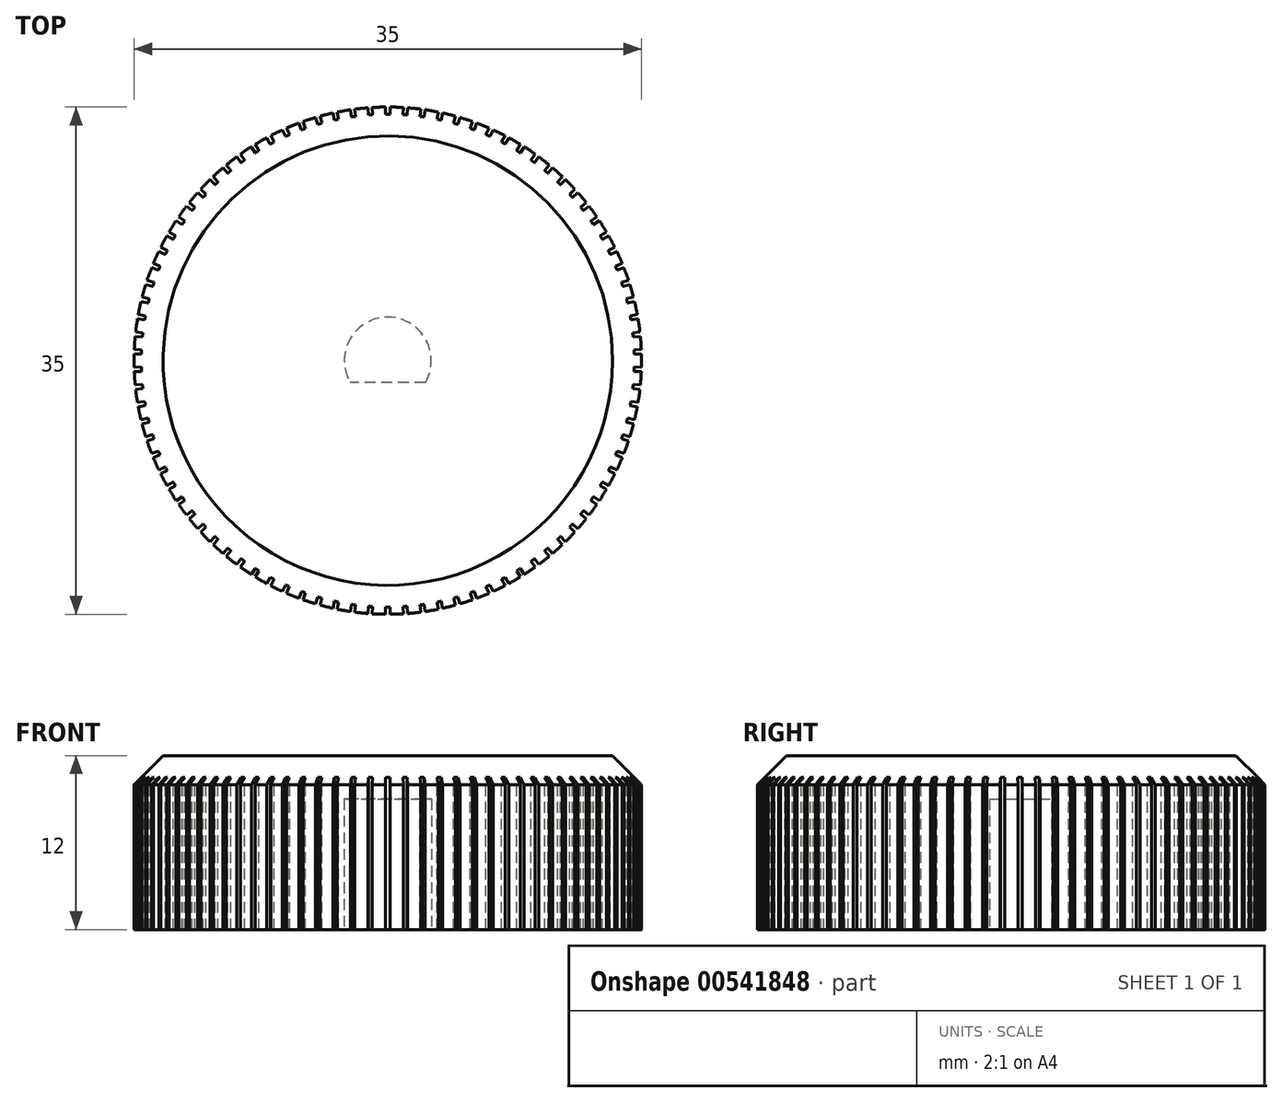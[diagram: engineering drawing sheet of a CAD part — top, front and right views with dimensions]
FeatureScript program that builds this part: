
annotation { "Feature Type Name" : "Feature", "Feature Type Description" : "" }
export const myFeature = defineFeature(function(context is Context, id is Id, definition is map)
    precondition{}
    {
        {
            var Q0;
            Q0=qCreatedBy(makeId("Top.planeOp"),FACE);
            var sketch = newSketch(context, id + "F0", { "sketchPlane" : qUnion([Q0])});
            skCircle(sketch, "E0", {"center": v(0, 0) * mm, "radius": 17.5 * mm});
            skSolve(sketch);
        }
        {
            var Q0;
            Q0=makeQuery(id+"F0.imprint","IMPRINT",FACE,{"disambiguationData":[TD([[makeQuery(id+"F0.imprint","IMPRINT",EDGE,{"derivedFrom":sQuery(id+"F0.wireOp",EDGE,"E0")}),1.0]])]});
            extrude(context, id + "F1", {"entities" : qUnion([Q0]), "depth" : 12 * mm, "offsetDistance" : 25 * mm});
        }
        {
            var Q0;
            Q0=makeQuery(id+"F1.opExtrude","CAP_EDGE",EDGE,{"disambiguationData":[OSD([sQuery(id+"F0.wireOp",EDGE,"E0")])],"isStart":false});
            chamfer(context, id + "F2", {"entities" : qUnion([Q0]), "width" : 2 * mm, "tangentPropagation" : true});
        }
        {
            var Q0;
            Q0=makeQuery(id+"F1.opExtrude","CAP_FACE",FACE,{"disambiguationData":[OSD([sQuery(id+"F0.wireOp",EDGE,"E0")])],"isStart":false});
            var sketch = newSketch(context, id + "F3", { "sketchPlane" : qUnion([Q0])});
            skLineSegment(sketch, "E1", {"start": v(0.15, 17) * mm, "end": v(0.17, 20) * mm});
            skLineSegment(sketch, "E2", {"start": v(0.17, 20) * mm, "end": v(-0.17, 20) * mm});
            skLineSegment(sketch, "E3", {"start": v(-0.17, 20) * mm, "end": v(-0.15, 17) * mm});
            skLineSegment(sketch, "E4.1.2", {"start": v(-0.17, -20) * mm, "end": v(0.17, -20) * mm});
            skPoint(sketch, "E4.center", {"position": v(0, 0) * mm});
            skLineSegment(sketch, "E5", {"start": v(0.15, 17) * mm, "end": v(-0.15, 17) * mm});
            skLineSegment(sketch, "E6.1.0", {"start": v(-1.04, 16.97) * mm, "end": v(-1.22, 19.96) * mm});
            skLineSegment(sketch, "E6.1.1", {"start": v(-1.04, 16.97) * mm, "end": v(-1.33, 16.95) * mm});
            skLineSegment(sketch, "E6.1.2", {"start": v(-1.57, 19.94) * mm, "end": v(-1.33, 16.95) * mm});
            skLineSegment(sketch, "E6.1.3", {"start": v(-1.22, 19.96) * mm, "end": v(-1.57, 19.94) * mm});
            skLineSegment(sketch, "E6.2.0", {"start": v(-2.22, 16.85) * mm, "end": v(-2.61, 19.83) * mm});
            skLineSegment(sketch, "E6.2.1", {"start": v(-2.22, 16.85) * mm, "end": v(-2.51, 16.82) * mm});
            skLineSegment(sketch, "E6.2.2", {"start": v(-2.96, 19.78) * mm, "end": v(-2.51, 16.82) * mm});
            skLineSegment(sketch, "E6.2.3", {"start": v(-2.61, 19.83) * mm, "end": v(-2.96, 19.78) * mm});
            skLineSegment(sketch, "E6.3.0", {"start": v(-3.39, 16.66) * mm, "end": v(-3.99, 19.6) * mm});
            skLineSegment(sketch, "E6.3.1", {"start": v(-3.39, 16.66) * mm, "end": v(-3.68, 16.6) * mm});
            skLineSegment(sketch, "E6.3.2", {"start": v(-4.33, 19.53) * mm, "end": v(-3.68, 16.6) * mm});
            skLineSegment(sketch, "E6.3.3", {"start": v(-3.99, 19.6) * mm, "end": v(-4.33, 19.53) * mm});
            skLineSegment(sketch, "E6.4.0", {"start": v(-4.54, 16.38) * mm, "end": v(-5.34, 19.27) * mm});
            skLineSegment(sketch, "E6.4.1", {"start": v(-4.54, 16.38) * mm, "end": v(-4.83, 16.3) * mm});
            skLineSegment(sketch, "E6.4.2", {"start": v(-5.68, 19.18) * mm, "end": v(-4.83, 16.3) * mm});
            skLineSegment(sketch, "E6.4.3", {"start": v(-5.34, 19.27) * mm, "end": v(-5.68, 19.18) * mm});
            skLineSegment(sketch, "E6.5.0", {"start": v(-5.67, 16.02) * mm, "end": v(-6.68, 18.85) * mm});
            skLineSegment(sketch, "E6.5.1", {"start": v(-5.67, 16.02) * mm, "end": v(-5.95, 15.93) * mm});
            skLineSegment(sketch, "E6.5.2", {"start": v(-7, 18.73) * mm, "end": v(-5.95, 15.93) * mm});
            skLineSegment(sketch, "E6.5.3", {"start": v(-6.68, 18.85) * mm, "end": v(-7, 18.73) * mm});
            skLineSegment(sketch, "E6.6.0", {"start": v(-6.78, 15.6) * mm, "end": v(-7.97, 18.34) * mm});
            skLineSegment(sketch, "E6.6.1", {"start": v(-6.78, 15.6) * mm, "end": v(-7.05, 15.47) * mm});
            skLineSegment(sketch, "E6.6.2", {"start": v(-8.3, 18.2) * mm, "end": v(-7.05, 15.47) * mm});
            skLineSegment(sketch, "E6.6.3", {"start": v(-7.97, 18.34) * mm, "end": v(-8.3, 18.2) * mm});
            skLineSegment(sketch, "E6.7.0", {"start": v(-7.85, 15.08) * mm, "end": v(-9.23, 17.74) * mm});
            skLineSegment(sketch, "E6.7.1", {"start": v(-7.85, 15.08) * mm, "end": v(-8.11, 14.94) * mm});
            skLineSegment(sketch, "E6.7.2", {"start": v(-9.54, 17.58) * mm, "end": v(-8.11, 14.94) * mm});
            skLineSegment(sketch, "E6.7.3", {"start": v(-9.23, 17.74) * mm, "end": v(-9.54, 17.58) * mm});
            skLineSegment(sketch, "E6.8.0", {"start": v(-8.88, 14.5) * mm, "end": v(-10.45, 17.05) * mm});
            skLineSegment(sketch, "E6.8.1", {"start": v(-8.88, 14.5) * mm, "end": v(-9.14, 14.34) * mm});
            skLineSegment(sketch, "E6.8.2", {"start": v(-10.75, 16.87) * mm, "end": v(-9.14, 14.34) * mm});
            skLineSegment(sketch, "E6.8.3", {"start": v(-10.45, 17.05) * mm, "end": v(-10.75, 16.87) * mm});
            skLineSegment(sketch, "E6.9.0", {"start": v(-9.87, 13.84) * mm, "end": v(-11.61, 16.28) * mm});
            skLineSegment(sketch, "E6.9.1", {"start": v(-9.87, 13.84) * mm, "end": v(-10.11, 13.67) * mm});
            skLineSegment(sketch, "E6.9.2", {"start": v(-11.9, 16.08) * mm, "end": v(-10.11, 13.67) * mm});
            skLineSegment(sketch, "E6.9.3", {"start": v(-11.61, 16.28) * mm, "end": v(-11.9, 16.08) * mm});
            skLineSegment(sketch, "E6.10.0", {"start": v(-10.81, 13.12) * mm, "end": v(-12.72, 15.43) * mm});
            skLineSegment(sketch, "E6.10.1", {"start": v(-10.81, 13.12) * mm, "end": v(-11.04, 12.93) * mm});
            skLineSegment(sketch, "E6.10.2", {"start": v(-12.99, 15.2) * mm, "end": v(-11.04, 12.93) * mm});
            skLineSegment(sketch, "E6.10.3", {"start": v(-12.72, 15.43) * mm, "end": v(-12.99, 15.2) * mm});
            skLineSegment(sketch, "E6.11.0", {"start": v(-11.7, 12.33) * mm, "end": v(-13.77, 14.5) * mm});
            skLineSegment(sketch, "E6.11.1", {"start": v(-11.7, 12.33) * mm, "end": v(-11.92, 12.13) * mm});
            skLineSegment(sketch, "E6.11.2", {"start": v(-14.02, 14.27) * mm, "end": v(-11.92, 12.13) * mm});
            skLineSegment(sketch, "E6.11.3", {"start": v(-13.77, 14.5) * mm, "end": v(-14.02, 14.27) * mm});
            skLineSegment(sketch, "E6.12.0", {"start": v(-12.53, 11.49) * mm, "end": v(-14.75, 13.51) * mm});
            skLineSegment(sketch, "E6.12.1", {"start": v(-12.53, 11.49) * mm, "end": v(-12.73, 11.27) * mm});
            skLineSegment(sketch, "E6.12.2", {"start": v(-14.98, 13.25) * mm, "end": v(-12.73, 11.27) * mm});
            skLineSegment(sketch, "E6.12.3", {"start": v(-14.75, 13.51) * mm, "end": v(-14.98, 13.25) * mm});
            skLineSegment(sketch, "E6.13.0", {"start": v(-13.3, 10.58) * mm, "end": v(-15.65, 12.45) * mm});
            skLineSegment(sketch, "E6.13.1", {"start": v(-13.3, 10.58) * mm, "end": v(-13.49, 10.35) * mm});
            skLineSegment(sketch, "E6.13.2", {"start": v(-15.87, 12.18) * mm, "end": v(-13.49, 10.35) * mm});
            skLineSegment(sketch, "E6.13.3", {"start": v(-15.65, 12.45) * mm, "end": v(-15.87, 12.18) * mm});
            skLineSegment(sketch, "E6.14.0", {"start": v(-14.01, 9.63) * mm, "end": v(-16.48, 11.33) * mm});
            skLineSegment(sketch, "E6.14.1", {"start": v(-14.01, 9.63) * mm, "end": v(-14.18, 9.38) * mm});
            skLineSegment(sketch, "E6.14.2", {"start": v(-16.68, 11.04) * mm, "end": v(-14.18, 9.38) * mm});
            skLineSegment(sketch, "E6.14.3", {"start": v(-16.48, 11.33) * mm, "end": v(-16.68, 11.04) * mm});
            skLineSegment(sketch, "E6.15.0", {"start": v(-14.65, 8.63) * mm, "end": v(-17.23, 10.15) * mm});
            skLineSegment(sketch, "E6.15.1", {"start": v(-14.65, 8.63) * mm, "end": v(-14.8, 8.37) * mm});
            skLineSegment(sketch, "E6.15.2", {"start": v(-17.4, 9.85) * mm, "end": v(-14.8, 8.37) * mm});
            skLineSegment(sketch, "E6.15.3", {"start": v(-17.23, 10.15) * mm, "end": v(-17.4, 9.85) * mm});
            skLineSegment(sketch, "E6.16.0", {"start": v(-15.21, 7.59) * mm, "end": v(-17.9, 8.92) * mm});
            skLineSegment(sketch, "E6.16.1", {"start": v(-15.21, 7.59) * mm, "end": v(-15.35, 7.32) * mm});
            skLineSegment(sketch, "E6.16.2", {"start": v(-18.05, 8.61) * mm, "end": v(-15.35, 7.32) * mm});
            skLineSegment(sketch, "E6.16.3", {"start": v(-17.9, 8.92) * mm, "end": v(-18.05, 8.61) * mm});
            skLineSegment(sketch, "E6.17.0", {"start": v(-15.7, 6.5) * mm, "end": v(-18.48, 7.65) * mm});
            skLineSegment(sketch, "E6.17.1", {"start": v(-15.7, 6.5) * mm, "end": v(-15.82, 6.23) * mm});
            skLineSegment(sketch, "E6.17.2", {"start": v(-18.6, 7.33) * mm, "end": v(-15.82, 6.23) * mm});
            skLineSegment(sketch, "E6.17.3", {"start": v(-18.48, 7.65) * mm, "end": v(-18.6, 7.33) * mm});
            skLineSegment(sketch, "E6.18.0", {"start": v(-16.12, 5.4) * mm, "end": v(-18.97, 6.35) * mm});
            skLineSegment(sketch, "E6.18.1", {"start": v(-16.12, 5.4) * mm, "end": v(-16.22, 5.11) * mm});
            skLineSegment(sketch, "E6.18.2", {"start": v(-19.07, 6.01) * mm, "end": v(-16.22, 5.11) * mm});
            skLineSegment(sketch, "E6.18.3", {"start": v(-18.97, 6.35) * mm, "end": v(-19.07, 6.01) * mm});
            skLineSegment(sketch, "E6.19.0", {"start": v(-16.46, 4.26) * mm, "end": v(-19.36, 5) * mm});
            skLineSegment(sketch, "E6.19.1", {"start": v(-16.46, 4.26) * mm, "end": v(-16.53, 3.97) * mm});
            skLineSegment(sketch, "E6.19.2", {"start": v(-19.45, 4.67) * mm, "end": v(-16.53, 3.97) * mm});
            skLineSegment(sketch, "E6.19.3", {"start": v(-19.36, 5) * mm, "end": v(-19.45, 4.67) * mm});
            skLineSegment(sketch, "E6.20.0", {"start": v(-16.72, 3.1) * mm, "end": v(-19.67, 3.64) * mm});
            skLineSegment(sketch, "E6.20.1", {"start": v(-16.72, 3.1) * mm, "end": v(-16.77, 2.8) * mm});
            skLineSegment(sketch, "E6.20.2", {"start": v(-19.73, 3.3) * mm, "end": v(-16.77, 2.8) * mm});
            skLineSegment(sketch, "E6.20.3", {"start": v(-19.67, 3.64) * mm, "end": v(-19.73, 3.3) * mm});
            skLineSegment(sketch, "E6.21.0", {"start": v(-16.9, 1.92) * mm, "end": v(-19.87, 2.26) * mm});
            skLineSegment(sketch, "E6.21.1", {"start": v(-16.9, 1.92) * mm, "end": v(-16.92, 1.63) * mm});
            skLineSegment(sketch, "E6.21.2", {"start": v(-19.9, 1.92) * mm, "end": v(-16.92, 1.63) * mm});
            skLineSegment(sketch, "E6.21.3", {"start": v(-19.87, 2.26) * mm, "end": v(-19.9, 1.92) * mm});
            skLineSegment(sketch, "E6.22.0", {"start": v(-16.98, 0.74) * mm, "end": v(-19.98, 0.87) * mm});
            skLineSegment(sketch, "E6.22.1", {"start": v(-16.98, 0.74) * mm, "end": v(-17, 0.45) * mm});
            skLineSegment(sketch, "E6.22.2", {"start": v(-20, 0.52) * mm, "end": v(-17, 0.45) * mm});
            skLineSegment(sketch, "E6.22.3", {"start": v(-19.98, 0.87) * mm, "end": v(-20, 0.52) * mm});
            skLineSegment(sketch, "E6.23.0", {"start": v(-17, -0.45) * mm, "end": v(-20, -0.52) * mm});
            skLineSegment(sketch, "E6.23.1", {"start": v(-17, -0.45) * mm, "end": v(-16.99, -0.74) * mm});
            skLineSegment(sketch, "E6.23.2", {"start": v(-19.98, -0.87) * mm, "end": v(-16.99, -0.74) * mm});
            skLineSegment(sketch, "E6.23.3", {"start": v(-20, -0.52) * mm, "end": v(-19.98, -0.87) * mm});
            skLineSegment(sketch, "E6.24.0", {"start": v(-16.92, -1.63) * mm, "end": v(-19.9, -1.92) * mm});
            skLineSegment(sketch, "E6.24.1", {"start": v(-16.92, -1.63) * mm, "end": v(-16.9, -1.92) * mm});
            skLineSegment(sketch, "E6.24.2", {"start": v(-19.87, -2.26) * mm, "end": v(-16.9, -1.92) * mm});
            skLineSegment(sketch, "E6.24.3", {"start": v(-19.9, -1.92) * mm, "end": v(-19.87, -2.26) * mm});
            skLineSegment(sketch, "E6.25.0", {"start": v(-16.77, -2.8) * mm, "end": v(-19.73, -3.3) * mm});
            skLineSegment(sketch, "E6.25.1", {"start": v(-16.77, -2.8) * mm, "end": v(-16.72, -3.1) * mm});
            skLineSegment(sketch, "E6.25.2", {"start": v(-19.67, -3.64) * mm, "end": v(-16.72, -3.1) * mm});
            skLineSegment(sketch, "E6.25.3", {"start": v(-19.73, -3.3) * mm, "end": v(-19.67, -3.64) * mm});
            skLineSegment(sketch, "E6.26.0", {"start": v(-16.53, -3.97) * mm, "end": v(-19.45, -4.67) * mm});
            skLineSegment(sketch, "E6.26.1", {"start": v(-16.53, -3.97) * mm, "end": v(-16.46, -4.26) * mm});
            skLineSegment(sketch, "E6.26.2", {"start": v(-19.36, -5) * mm, "end": v(-16.46, -4.26) * mm});
            skLineSegment(sketch, "E6.26.3", {"start": v(-19.45, -4.67) * mm, "end": v(-19.36, -5) * mm});
            skLineSegment(sketch, "E6.27.0", {"start": v(-16.21, -5.11) * mm, "end": v(-19.07, -6.01) * mm});
            skLineSegment(sketch, "E6.27.1", {"start": v(-16.21, -5.11) * mm, "end": v(-16.12, -5.4) * mm});
            skLineSegment(sketch, "E6.27.2", {"start": v(-18.97, -6.35) * mm, "end": v(-16.12, -5.4) * mm});
            skLineSegment(sketch, "E6.27.3", {"start": v(-19.07, -6.01) * mm, "end": v(-18.97, -6.35) * mm});
            skLineSegment(sketch, "E6.28.0", {"start": v(-15.82, -6.23) * mm, "end": v(-18.6, -7.33) * mm});
            skLineSegment(sketch, "E6.28.1", {"start": v(-15.82, -6.23) * mm, "end": v(-15.7, -6.5) * mm});
            skLineSegment(sketch, "E6.28.2", {"start": v(-18.48, -7.65) * mm, "end": v(-15.7, -6.5) * mm});
            skLineSegment(sketch, "E6.28.3", {"start": v(-18.6, -7.33) * mm, "end": v(-18.48, -7.65) * mm});
            skLineSegment(sketch, "E6.29.0", {"start": v(-15.34, -7.32) * mm, "end": v(-18.05, -8.61) * mm});
            skLineSegment(sketch, "E6.29.1", {"start": v(-15.34, -7.32) * mm, "end": v(-15.22, -7.59) * mm});
            skLineSegment(sketch, "E6.29.2", {"start": v(-17.9, -8.92) * mm, "end": v(-15.22, -7.59) * mm});
            skLineSegment(sketch, "E6.29.3", {"start": v(-18.05, -8.61) * mm, "end": v(-17.9, -8.92) * mm});
            skLineSegment(sketch, "E6.30.0", {"start": v(-14.8, -8.37) * mm, "end": v(-17.4, -9.85) * mm});
            skLineSegment(sketch, "E6.30.1", {"start": v(-14.8, -8.37) * mm, "end": v(-14.65, -8.63) * mm});
            skLineSegment(sketch, "E6.30.2", {"start": v(-17.23, -10.15) * mm, "end": v(-14.65, -8.63) * mm});
            skLineSegment(sketch, "E6.30.3", {"start": v(-17.4, -9.85) * mm, "end": v(-17.23, -10.15) * mm});
            skLineSegment(sketch, "E6.31.0", {"start": v(-14.18, -9.38) * mm, "end": v(-16.68, -11.04) * mm});
            skLineSegment(sketch, "E6.31.1", {"start": v(-14.18, -9.38) * mm, "end": v(-14.01, -9.63) * mm});
            skLineSegment(sketch, "E6.31.2", {"start": v(-16.48, -11.33) * mm, "end": v(-14.01, -9.63) * mm});
            skLineSegment(sketch, "E6.31.3", {"start": v(-16.68, -11.04) * mm, "end": v(-16.48, -11.33) * mm});
            skLineSegment(sketch, "E6.32.0", {"start": v(-13.49, -10.35) * mm, "end": v(-15.87, -12.18) * mm});
            skLineSegment(sketch, "E6.32.1", {"start": v(-13.49, -10.35) * mm, "end": v(-13.3, -10.58) * mm});
            skLineSegment(sketch, "E6.32.2", {"start": v(-15.65, -12.45) * mm, "end": v(-13.3, -10.58) * mm});
            skLineSegment(sketch, "E6.32.3", {"start": v(-15.87, -12.18) * mm, "end": v(-15.65, -12.45) * mm});
            skLineSegment(sketch, "E6.33.0", {"start": v(-12.73, -11.26) * mm, "end": v(-14.98, -13.25) * mm});
            skLineSegment(sketch, "E6.33.1", {"start": v(-12.73, -11.26) * mm, "end": v(-12.54, -11.49) * mm});
            skLineSegment(sketch, "E6.33.2", {"start": v(-14.75, -13.51) * mm, "end": v(-12.54, -11.49) * mm});
            skLineSegment(sketch, "E6.33.3", {"start": v(-14.98, -13.25) * mm, "end": v(-14.75, -13.51) * mm});
            skLineSegment(sketch, "E6.34.0", {"start": v(-11.92, -12.13) * mm, "end": v(-14.02, -14.27) * mm});
            skLineSegment(sketch, "E6.34.1", {"start": v(-11.92, -12.13) * mm, "end": v(-11.7, -12.33) * mm});
            skLineSegment(sketch, "E6.34.2", {"start": v(-13.77, -14.5) * mm, "end": v(-11.7, -12.33) * mm});
            skLineSegment(sketch, "E6.34.3", {"start": v(-14.02, -14.27) * mm, "end": v(-13.77, -14.5) * mm});
            skLineSegment(sketch, "E6.35.0", {"start": v(-11.04, -12.93) * mm, "end": v(-12.99, -15.2) * mm});
            skLineSegment(sketch, "E6.35.1", {"start": v(-11.04, -12.93) * mm, "end": v(-10.81, -13.12) * mm});
            skLineSegment(sketch, "E6.35.2", {"start": v(-12.72, -15.43) * mm, "end": v(-10.81, -13.12) * mm});
            skLineSegment(sketch, "E6.35.3", {"start": v(-12.99, -15.2) * mm, "end": v(-12.72, -15.43) * mm});
            skLineSegment(sketch, "E6.36.0", {"start": v(-10.11, -13.67) * mm, "end": v(-11.9, -16.08) * mm});
            skLineSegment(sketch, "E6.36.1", {"start": v(-10.11, -13.67) * mm, "end": v(-9.87, -13.84) * mm});
            skLineSegment(sketch, "E6.36.2", {"start": v(-11.61, -16.28) * mm, "end": v(-9.87, -13.84) * mm});
            skLineSegment(sketch, "E6.36.3", {"start": v(-11.9, -16.08) * mm, "end": v(-11.61, -16.28) * mm});
            skLineSegment(sketch, "E6.37.0", {"start": v(-9.13, -14.34) * mm, "end": v(-10.75, -16.87) * mm});
            skLineSegment(sketch, "E6.37.1", {"start": v(-9.13, -14.34) * mm, "end": v(-8.88, -14.5) * mm});
            skLineSegment(sketch, "E6.37.2", {"start": v(-10.45, -17.05) * mm, "end": v(-8.88, -14.5) * mm});
            skLineSegment(sketch, "E6.37.3", {"start": v(-10.75, -16.87) * mm, "end": v(-10.45, -17.05) * mm});
            skLineSegment(sketch, "E6.38.0", {"start": v(-8.11, -14.94) * mm, "end": v(-9.54, -17.58) * mm});
            skLineSegment(sketch, "E6.38.1", {"start": v(-8.11, -14.94) * mm, "end": v(-7.85, -15.08) * mm});
            skLineSegment(sketch, "E6.38.2", {"start": v(-9.23, -17.74) * mm, "end": v(-7.85, -15.08) * mm});
            skLineSegment(sketch, "E6.38.3", {"start": v(-9.54, -17.58) * mm, "end": v(-9.23, -17.74) * mm});
            skLineSegment(sketch, "E6.39.0", {"start": v(-7.05, -15.47) * mm, "end": v(-8.3, -18.2) * mm});
            skLineSegment(sketch, "E6.39.1", {"start": v(-7.05, -15.47) * mm, "end": v(-6.78, -15.6) * mm});
            skLineSegment(sketch, "E6.39.2", {"start": v(-7.97, -18.34) * mm, "end": v(-6.78, -15.6) * mm});
            skLineSegment(sketch, "E6.39.3", {"start": v(-8.3, -18.2) * mm, "end": v(-7.97, -18.34) * mm});
            skLineSegment(sketch, "E6.40.0", {"start": v(-5.95, -15.92) * mm, "end": v(-7, -18.73) * mm});
            skLineSegment(sketch, "E6.40.1", {"start": v(-5.95, -15.92) * mm, "end": v(-5.68, -16.03) * mm});
            skLineSegment(sketch, "E6.40.2", {"start": v(-6.68, -18.85) * mm, "end": v(-5.68, -16.03) * mm});
            skLineSegment(sketch, "E6.40.3", {"start": v(-7, -18.73) * mm, "end": v(-6.68, -18.85) * mm});
            skLineSegment(sketch, "E6.41.0", {"start": v(-4.83, -16.3) * mm, "end": v(-5.68, -19.18) * mm});
            skLineSegment(sketch, "E6.41.1", {"start": v(-4.83, -16.3) * mm, "end": v(-4.54, -16.38) * mm});
            skLineSegment(sketch, "E6.41.2", {"start": v(-5.34, -19.27) * mm, "end": v(-4.54, -16.38) * mm});
            skLineSegment(sketch, "E6.41.3", {"start": v(-5.68, -19.18) * mm, "end": v(-5.34, -19.27) * mm});
            skLineSegment(sketch, "E6.42.0", {"start": v(-3.68, -16.6) * mm, "end": v(-4.33, -19.53) * mm});
            skLineSegment(sketch, "E6.42.1", {"start": v(-3.68, -16.6) * mm, "end": v(-3.39, -16.66) * mm});
            skLineSegment(sketch, "E6.42.2", {"start": v(-3.99, -19.6) * mm, "end": v(-3.39, -16.66) * mm});
            skLineSegment(sketch, "E6.42.3", {"start": v(-4.33, -19.53) * mm, "end": v(-3.99, -19.6) * mm});
            skLineSegment(sketch, "E6.43.0", {"start": v(-2.51, -16.81) * mm, "end": v(-2.96, -19.78) * mm});
            skLineSegment(sketch, "E6.43.1", {"start": v(-2.51, -16.81) * mm, "end": v(-2.22, -16.86) * mm});
            skLineSegment(sketch, "E6.43.2", {"start": v(-2.61, -19.83) * mm, "end": v(-2.22, -16.86) * mm});
            skLineSegment(sketch, "E6.43.3", {"start": v(-2.96, -19.78) * mm, "end": v(-2.61, -19.83) * mm});
            skLineSegment(sketch, "E6.44.0", {"start": v(-1.33, -16.95) * mm, "end": v(-1.57, -19.94) * mm});
            skLineSegment(sketch, "E6.44.1", {"start": v(-1.33, -16.95) * mm, "end": v(-1.04, -16.97) * mm});
            skLineSegment(sketch, "E6.44.2", {"start": v(-1.22, -19.96) * mm, "end": v(-1.04, -16.97) * mm});
            skLineSegment(sketch, "E6.44.3", {"start": v(-1.57, -19.94) * mm, "end": v(-1.22, -19.96) * mm});
            skLineSegment(sketch, "E6.45.0", {"start": v(-0.15, -17) * mm, "end": v(-0.17, -20) * mm});
            skLineSegment(sketch, "E6.45.1", {"start": v(-0.15, -17) * mm, "end": v(0.15, -17) * mm});
            skLineSegment(sketch, "E6.45.2", {"start": v(0.17, -20) * mm, "end": v(0.15, -17) * mm});
            skLineSegment(sketch, "E6.46.0", {"start": v(1.04, -16.97) * mm, "end": v(1.22, -19.96) * mm});
            skLineSegment(sketch, "E6.46.1", {"start": v(1.04, -16.97) * mm, "end": v(1.33, -16.95) * mm});
            skLineSegment(sketch, "E6.46.2", {"start": v(1.57, -19.94) * mm, "end": v(1.33, -16.95) * mm});
            skLineSegment(sketch, "E6.46.3", {"start": v(1.22, -19.96) * mm, "end": v(1.57, -19.94) * mm});
            skLineSegment(sketch, "E6.47.0", {"start": v(2.22, -16.85) * mm, "end": v(2.61, -19.83) * mm});
            skLineSegment(sketch, "E6.47.1", {"start": v(2.22, -16.85) * mm, "end": v(2.51, -16.82) * mm});
            skLineSegment(sketch, "E6.47.2", {"start": v(2.96, -19.78) * mm, "end": v(2.51, -16.82) * mm});
            skLineSegment(sketch, "E6.47.3", {"start": v(2.61, -19.83) * mm, "end": v(2.96, -19.78) * mm});
            skLineSegment(sketch, "E6.48.0", {"start": v(3.39, -16.66) * mm, "end": v(3.99, -19.6) * mm});
            skLineSegment(sketch, "E6.48.1", {"start": v(3.39, -16.66) * mm, "end": v(3.68, -16.6) * mm});
            skLineSegment(sketch, "E6.48.2", {"start": v(4.33, -19.53) * mm, "end": v(3.68, -16.6) * mm});
            skLineSegment(sketch, "E6.48.3", {"start": v(3.99, -19.6) * mm, "end": v(4.33, -19.53) * mm});
            skLineSegment(sketch, "E6.49.0", {"start": v(4.54, -16.38) * mm, "end": v(5.34, -19.27) * mm});
            skLineSegment(sketch, "E6.49.1", {"start": v(4.54, -16.38) * mm, "end": v(4.83, -16.3) * mm});
            skLineSegment(sketch, "E6.49.2", {"start": v(5.68, -19.18) * mm, "end": v(4.83, -16.3) * mm});
            skLineSegment(sketch, "E6.49.3", {"start": v(5.34, -19.27) * mm, "end": v(5.68, -19.18) * mm});
            skLineSegment(sketch, "E6.50.0", {"start": v(5.67, -16.02) * mm, "end": v(6.68, -18.85) * mm});
            skLineSegment(sketch, "E6.50.1", {"start": v(5.67, -16.02) * mm, "end": v(5.95, -15.93) * mm});
            skLineSegment(sketch, "E6.50.2", {"start": v(7, -18.73) * mm, "end": v(5.95, -15.93) * mm});
            skLineSegment(sketch, "E6.50.3", {"start": v(6.68, -18.85) * mm, "end": v(7, -18.73) * mm});
            skLineSegment(sketch, "E6.51.0", {"start": v(6.78, -15.6) * mm, "end": v(7.97, -18.34) * mm});
            skLineSegment(sketch, "E6.51.1", {"start": v(6.78, -15.6) * mm, "end": v(7.05, -15.47) * mm});
            skLineSegment(sketch, "E6.51.2", {"start": v(8.3, -18.2) * mm, "end": v(7.05, -15.47) * mm});
            skLineSegment(sketch, "E6.51.3", {"start": v(7.97, -18.34) * mm, "end": v(8.3, -18.2) * mm});
            skLineSegment(sketch, "E6.52.0", {"start": v(7.85, -15.08) * mm, "end": v(9.23, -17.74) * mm});
            skLineSegment(sketch, "E6.52.1", {"start": v(7.85, -15.08) * mm, "end": v(8.11, -14.94) * mm});
            skLineSegment(sketch, "E6.52.2", {"start": v(9.54, -17.58) * mm, "end": v(8.11, -14.94) * mm});
            skLineSegment(sketch, "E6.52.3", {"start": v(9.23, -17.74) * mm, "end": v(9.54, -17.58) * mm});
            skLineSegment(sketch, "E6.53.0", {"start": v(8.88, -14.5) * mm, "end": v(10.45, -17.05) * mm});
            skLineSegment(sketch, "E6.53.1", {"start": v(8.88, -14.5) * mm, "end": v(9.14, -14.34) * mm});
            skLineSegment(sketch, "E6.53.2", {"start": v(10.75, -16.87) * mm, "end": v(9.14, -14.34) * mm});
            skLineSegment(sketch, "E6.53.3", {"start": v(10.45, -17.05) * mm, "end": v(10.75, -16.87) * mm});
            skLineSegment(sketch, "E6.54.0", {"start": v(9.87, -13.84) * mm, "end": v(11.61, -16.28) * mm});
            skLineSegment(sketch, "E6.54.1", {"start": v(9.87, -13.84) * mm, "end": v(10.11, -13.67) * mm});
            skLineSegment(sketch, "E6.54.2", {"start": v(11.9, -16.08) * mm, "end": v(10.11, -13.67) * mm});
            skLineSegment(sketch, "E6.54.3", {"start": v(11.61, -16.28) * mm, "end": v(11.9, -16.08) * mm});
            skLineSegment(sketch, "E6.55.0", {"start": v(10.81, -13.12) * mm, "end": v(12.72, -15.43) * mm});
            skLineSegment(sketch, "E6.55.1", {"start": v(10.81, -13.12) * mm, "end": v(11.04, -12.93) * mm});
            skLineSegment(sketch, "E6.55.2", {"start": v(12.99, -15.2) * mm, "end": v(11.04, -12.93) * mm});
            skLineSegment(sketch, "E6.55.3", {"start": v(12.72, -15.43) * mm, "end": v(12.99, -15.2) * mm});
            skLineSegment(sketch, "E6.56.0", {"start": v(11.7, -12.33) * mm, "end": v(13.77, -14.5) * mm});
            skLineSegment(sketch, "E6.56.1", {"start": v(11.7, -12.33) * mm, "end": v(11.92, -12.13) * mm});
            skLineSegment(sketch, "E6.56.2", {"start": v(14.02, -14.27) * mm, "end": v(11.92, -12.13) * mm});
            skLineSegment(sketch, "E6.56.3", {"start": v(13.77, -14.5) * mm, "end": v(14.02, -14.27) * mm});
            skLineSegment(sketch, "E6.57.0", {"start": v(12.53, -11.49) * mm, "end": v(14.75, -13.51) * mm});
            skLineSegment(sketch, "E6.57.1", {"start": v(12.53, -11.49) * mm, "end": v(12.73, -11.27) * mm});
            skLineSegment(sketch, "E6.57.2", {"start": v(14.98, -13.25) * mm, "end": v(12.73, -11.27) * mm});
            skLineSegment(sketch, "E6.57.3", {"start": v(14.75, -13.51) * mm, "end": v(14.98, -13.25) * mm});
            skLineSegment(sketch, "E6.58.0", {"start": v(13.3, -10.58) * mm, "end": v(15.65, -12.45) * mm});
            skLineSegment(sketch, "E6.58.1", {"start": v(13.3, -10.58) * mm, "end": v(13.49, -10.35) * mm});
            skLineSegment(sketch, "E6.58.2", {"start": v(15.87, -12.18) * mm, "end": v(13.49, -10.35) * mm});
            skLineSegment(sketch, "E6.58.3", {"start": v(15.65, -12.45) * mm, "end": v(15.87, -12.18) * mm});
            skLineSegment(sketch, "E6.59.0", {"start": v(14.01, -9.63) * mm, "end": v(16.48, -11.33) * mm});
            skLineSegment(sketch, "E6.59.1", {"start": v(14.01, -9.63) * mm, "end": v(14.18, -9.38) * mm});
            skLineSegment(sketch, "E6.59.2", {"start": v(16.68, -11.04) * mm, "end": v(14.18, -9.38) * mm});
            skLineSegment(sketch, "E6.59.3", {"start": v(16.48, -11.33) * mm, "end": v(16.68, -11.04) * mm});
            skLineSegment(sketch, "E6.60.0", {"start": v(14.65, -8.63) * mm, "end": v(17.23, -10.15) * mm});
            skLineSegment(sketch, "E6.60.1", {"start": v(14.65, -8.63) * mm, "end": v(14.8, -8.37) * mm});
            skLineSegment(sketch, "E6.60.2", {"start": v(17.4, -9.85) * mm, "end": v(14.8, -8.37) * mm});
            skLineSegment(sketch, "E6.60.3", {"start": v(17.23, -10.15) * mm, "end": v(17.4, -9.85) * mm});
            skLineSegment(sketch, "E6.61.0", {"start": v(15.21, -7.59) * mm, "end": v(17.9, -8.92) * mm});
            skLineSegment(sketch, "E6.61.1", {"start": v(15.21, -7.59) * mm, "end": v(15.35, -7.32) * mm});
            skLineSegment(sketch, "E6.61.2", {"start": v(18.05, -8.61) * mm, "end": v(15.35, -7.32) * mm});
            skLineSegment(sketch, "E6.61.3", {"start": v(17.9, -8.92) * mm, "end": v(18.05, -8.61) * mm});
            skLineSegment(sketch, "E6.62.0", {"start": v(15.7, -6.5) * mm, "end": v(18.48, -7.65) * mm});
            skLineSegment(sketch, "E6.62.1", {"start": v(15.7, -6.5) * mm, "end": v(15.82, -6.23) * mm});
            skLineSegment(sketch, "E6.62.2", {"start": v(18.6, -7.33) * mm, "end": v(15.82, -6.23) * mm});
            skLineSegment(sketch, "E6.62.3", {"start": v(18.48, -7.65) * mm, "end": v(18.6, -7.33) * mm});
            skLineSegment(sketch, "E6.63.0", {"start": v(16.12, -5.4) * mm, "end": v(18.97, -6.35) * mm});
            skLineSegment(sketch, "E6.63.1", {"start": v(16.12, -5.4) * mm, "end": v(16.22, -5.11) * mm});
            skLineSegment(sketch, "E6.63.2", {"start": v(19.07, -6.01) * mm, "end": v(16.22, -5.11) * mm});
            skLineSegment(sketch, "E6.63.3", {"start": v(18.97, -6.35) * mm, "end": v(19.07, -6.01) * mm});
            skLineSegment(sketch, "E6.64.0", {"start": v(16.46, -4.26) * mm, "end": v(19.36, -5) * mm});
            skLineSegment(sketch, "E6.64.1", {"start": v(16.46, -4.26) * mm, "end": v(16.53, -3.97) * mm});
            skLineSegment(sketch, "E6.64.2", {"start": v(19.45, -4.67) * mm, "end": v(16.53, -3.97) * mm});
            skLineSegment(sketch, "E6.64.3", {"start": v(19.36, -5) * mm, "end": v(19.45, -4.67) * mm});
            skLineSegment(sketch, "E6.65.0", {"start": v(16.72, -3.1) * mm, "end": v(19.67, -3.64) * mm});
            skLineSegment(sketch, "E6.65.1", {"start": v(16.72, -3.1) * mm, "end": v(16.77, -2.8) * mm});
            skLineSegment(sketch, "E6.65.2", {"start": v(19.73, -3.3) * mm, "end": v(16.77, -2.8) * mm});
            skLineSegment(sketch, "E6.65.3", {"start": v(19.67, -3.64) * mm, "end": v(19.73, -3.3) * mm});
            skLineSegment(sketch, "E6.66.0", {"start": v(16.9, -1.92) * mm, "end": v(19.87, -2.26) * mm});
            skLineSegment(sketch, "E6.66.1", {"start": v(16.9, -1.92) * mm, "end": v(16.92, -1.63) * mm});
            skLineSegment(sketch, "E6.66.2", {"start": v(19.9, -1.92) * mm, "end": v(16.92, -1.63) * mm});
            skLineSegment(sketch, "E6.66.3", {"start": v(19.87, -2.26) * mm, "end": v(19.9, -1.92) * mm});
            skLineSegment(sketch, "E6.67.0", {"start": v(16.98, -0.74) * mm, "end": v(19.98, -0.87) * mm});
            skLineSegment(sketch, "E6.67.1", {"start": v(16.98, -0.74) * mm, "end": v(17, -0.45) * mm});
            skLineSegment(sketch, "E6.67.2", {"start": v(20, -0.52) * mm, "end": v(17, -0.45) * mm});
            skLineSegment(sketch, "E6.67.3", {"start": v(19.98, -0.87) * mm, "end": v(20, -0.52) * mm});
            skLineSegment(sketch, "E6.68.0", {"start": v(17, 0.45) * mm, "end": v(20, 0.52) * mm});
            skLineSegment(sketch, "E6.68.1", {"start": v(17, 0.45) * mm, "end": v(16.99, 0.74) * mm});
            skLineSegment(sketch, "E6.68.2", {"start": v(19.98, 0.87) * mm, "end": v(16.99, 0.74) * mm});
            skLineSegment(sketch, "E6.68.3", {"start": v(20, 0.52) * mm, "end": v(19.98, 0.87) * mm});
            skLineSegment(sketch, "E6.69.0", {"start": v(16.92, 1.63) * mm, "end": v(19.9, 1.92) * mm});
            skLineSegment(sketch, "E6.69.1", {"start": v(16.92, 1.63) * mm, "end": v(16.9, 1.92) * mm});
            skLineSegment(sketch, "E6.69.2", {"start": v(19.87, 2.26) * mm, "end": v(16.9, 1.92) * mm});
            skLineSegment(sketch, "E6.69.3", {"start": v(19.9, 1.92) * mm, "end": v(19.87, 2.26) * mm});
            skLineSegment(sketch, "E6.70.0", {"start": v(16.77, 2.8) * mm, "end": v(19.73, 3.3) * mm});
            skLineSegment(sketch, "E6.70.1", {"start": v(16.77, 2.8) * mm, "end": v(16.72, 3.1) * mm});
            skLineSegment(sketch, "E6.70.2", {"start": v(19.67, 3.64) * mm, "end": v(16.72, 3.1) * mm});
            skLineSegment(sketch, "E6.70.3", {"start": v(19.73, 3.3) * mm, "end": v(19.67, 3.64) * mm});
            skLineSegment(sketch, "E6.71.0", {"start": v(16.53, 3.97) * mm, "end": v(19.45, 4.67) * mm});
            skLineSegment(sketch, "E6.71.1", {"start": v(16.53, 3.97) * mm, "end": v(16.46, 4.26) * mm});
            skLineSegment(sketch, "E6.71.2", {"start": v(19.36, 5) * mm, "end": v(16.46, 4.26) * mm});
            skLineSegment(sketch, "E6.71.3", {"start": v(19.45, 4.67) * mm, "end": v(19.36, 5) * mm});
            skLineSegment(sketch, "E6.72.0", {"start": v(16.21, 5.11) * mm, "end": v(19.07, 6.01) * mm});
            skLineSegment(sketch, "E6.72.1", {"start": v(16.21, 5.11) * mm, "end": v(16.12, 5.4) * mm});
            skLineSegment(sketch, "E6.72.2", {"start": v(18.97, 6.35) * mm, "end": v(16.12, 5.4) * mm});
            skLineSegment(sketch, "E6.72.3", {"start": v(19.07, 6.01) * mm, "end": v(18.97, 6.35) * mm});
            skLineSegment(sketch, "E6.73.0", {"start": v(15.82, 6.23) * mm, "end": v(18.6, 7.33) * mm});
            skLineSegment(sketch, "E6.73.1", {"start": v(15.82, 6.23) * mm, "end": v(15.7, 6.5) * mm});
            skLineSegment(sketch, "E6.73.2", {"start": v(18.48, 7.65) * mm, "end": v(15.7, 6.5) * mm});
            skLineSegment(sketch, "E6.73.3", {"start": v(18.6, 7.33) * mm, "end": v(18.48, 7.65) * mm});
            skLineSegment(sketch, "E6.74.0", {"start": v(15.34, 7.32) * mm, "end": v(18.05, 8.61) * mm});
            skLineSegment(sketch, "E6.74.1", {"start": v(15.34, 7.32) * mm, "end": v(15.22, 7.59) * mm});
            skLineSegment(sketch, "E6.74.2", {"start": v(17.9, 8.92) * mm, "end": v(15.22, 7.59) * mm});
            skLineSegment(sketch, "E6.74.3", {"start": v(18.05, 8.61) * mm, "end": v(17.9, 8.92) * mm});
            skLineSegment(sketch, "E6.75.0", {"start": v(14.8, 8.37) * mm, "end": v(17.4, 9.85) * mm});
            skLineSegment(sketch, "E6.75.1", {"start": v(14.8, 8.37) * mm, "end": v(14.65, 8.63) * mm});
            skLineSegment(sketch, "E6.75.2", {"start": v(17.23, 10.15) * mm, "end": v(14.65, 8.63) * mm});
            skLineSegment(sketch, "E6.75.3", {"start": v(17.4, 9.85) * mm, "end": v(17.23, 10.15) * mm});
            skLineSegment(sketch, "E6.76.0", {"start": v(14.18, 9.38) * mm, "end": v(16.68, 11.04) * mm});
            skLineSegment(sketch, "E6.76.1", {"start": v(14.18, 9.38) * mm, "end": v(14.01, 9.63) * mm});
            skLineSegment(sketch, "E6.76.2", {"start": v(16.48, 11.33) * mm, "end": v(14.01, 9.63) * mm});
            skLineSegment(sketch, "E6.76.3", {"start": v(16.68, 11.04) * mm, "end": v(16.48, 11.33) * mm});
            skLineSegment(sketch, "E6.77.0", {"start": v(13.49, 10.35) * mm, "end": v(15.87, 12.18) * mm});
            skLineSegment(sketch, "E6.77.1", {"start": v(13.49, 10.35) * mm, "end": v(13.3, 10.58) * mm});
            skLineSegment(sketch, "E6.77.2", {"start": v(15.65, 12.45) * mm, "end": v(13.3, 10.58) * mm});
            skLineSegment(sketch, "E6.77.3", {"start": v(15.87, 12.18) * mm, "end": v(15.65, 12.45) * mm});
            skLineSegment(sketch, "E6.78.0", {"start": v(12.73, 11.26) * mm, "end": v(14.98, 13.25) * mm});
            skLineSegment(sketch, "E6.78.1", {"start": v(12.73, 11.26) * mm, "end": v(12.54, 11.49) * mm});
            skLineSegment(sketch, "E6.78.2", {"start": v(14.75, 13.51) * mm, "end": v(12.54, 11.49) * mm});
            skLineSegment(sketch, "E6.78.3", {"start": v(14.98, 13.25) * mm, "end": v(14.75, 13.51) * mm});
            skLineSegment(sketch, "E6.79.0", {"start": v(11.92, 12.13) * mm, "end": v(14.02, 14.27) * mm});
            skLineSegment(sketch, "E6.79.1", {"start": v(11.92, 12.13) * mm, "end": v(11.7, 12.33) * mm});
            skLineSegment(sketch, "E6.79.2", {"start": v(13.77, 14.5) * mm, "end": v(11.7, 12.33) * mm});
            skLineSegment(sketch, "E6.79.3", {"start": v(14.02, 14.27) * mm, "end": v(13.77, 14.5) * mm});
            skLineSegment(sketch, "E6.80.0", {"start": v(11.04, 12.93) * mm, "end": v(12.99, 15.2) * mm});
            skLineSegment(sketch, "E6.80.1", {"start": v(11.04, 12.93) * mm, "end": v(10.81, 13.12) * mm});
            skLineSegment(sketch, "E6.80.2", {"start": v(12.72, 15.43) * mm, "end": v(10.81, 13.12) * mm});
            skLineSegment(sketch, "E6.80.3", {"start": v(12.99, 15.2) * mm, "end": v(12.72, 15.43) * mm});
            skLineSegment(sketch, "E6.81.0", {"start": v(10.11, 13.67) * mm, "end": v(11.9, 16.08) * mm});
            skLineSegment(sketch, "E6.81.1", {"start": v(10.11, 13.67) * mm, "end": v(9.87, 13.84) * mm});
            skLineSegment(sketch, "E6.81.2", {"start": v(11.61, 16.28) * mm, "end": v(9.87, 13.84) * mm});
            skLineSegment(sketch, "E6.81.3", {"start": v(11.9, 16.08) * mm, "end": v(11.61, 16.28) * mm});
            skLineSegment(sketch, "E6.82.0", {"start": v(9.13, 14.34) * mm, "end": v(10.75, 16.87) * mm});
            skLineSegment(sketch, "E6.82.1", {"start": v(9.13, 14.34) * mm, "end": v(8.88, 14.5) * mm});
            skLineSegment(sketch, "E6.82.2", {"start": v(10.45, 17.05) * mm, "end": v(8.88, 14.5) * mm});
            skLineSegment(sketch, "E6.82.3", {"start": v(10.75, 16.87) * mm, "end": v(10.45, 17.05) * mm});
            skLineSegment(sketch, "E6.83.0", {"start": v(8.11, 14.94) * mm, "end": v(9.54, 17.58) * mm});
            skLineSegment(sketch, "E6.83.1", {"start": v(8.11, 14.94) * mm, "end": v(7.85, 15.08) * mm});
            skLineSegment(sketch, "E6.83.2", {"start": v(9.23, 17.74) * mm, "end": v(7.85, 15.08) * mm});
            skLineSegment(sketch, "E6.83.3", {"start": v(9.54, 17.58) * mm, "end": v(9.23, 17.74) * mm});
            skLineSegment(sketch, "E6.84.0", {"start": v(7.05, 15.47) * mm, "end": v(8.3, 18.2) * mm});
            skLineSegment(sketch, "E6.84.1", {"start": v(7.05, 15.47) * mm, "end": v(6.78, 15.6) * mm});
            skLineSegment(sketch, "E6.84.2", {"start": v(7.97, 18.34) * mm, "end": v(6.78, 15.6) * mm});
            skLineSegment(sketch, "E6.84.3", {"start": v(8.3, 18.2) * mm, "end": v(7.97, 18.34) * mm});
            skLineSegment(sketch, "E6.85.0", {"start": v(5.95, 15.92) * mm, "end": v(7, 18.73) * mm});
            skLineSegment(sketch, "E6.85.1", {"start": v(5.95, 15.92) * mm, "end": v(5.68, 16.03) * mm});
            skLineSegment(sketch, "E6.85.2", {"start": v(6.68, 18.85) * mm, "end": v(5.68, 16.03) * mm});
            skLineSegment(sketch, "E6.85.3", {"start": v(7, 18.73) * mm, "end": v(6.68, 18.85) * mm});
            skLineSegment(sketch, "E6.86.0", {"start": v(4.83, 16.3) * mm, "end": v(5.68, 19.18) * mm});
            skLineSegment(sketch, "E6.86.1", {"start": v(4.83, 16.3) * mm, "end": v(4.54, 16.38) * mm});
            skLineSegment(sketch, "E6.86.2", {"start": v(5.34, 19.27) * mm, "end": v(4.54, 16.38) * mm});
            skLineSegment(sketch, "E6.86.3", {"start": v(5.68, 19.18) * mm, "end": v(5.34, 19.27) * mm});
            skLineSegment(sketch, "E6.87.0", {"start": v(3.68, 16.6) * mm, "end": v(4.33, 19.53) * mm});
            skLineSegment(sketch, "E6.87.1", {"start": v(3.68, 16.6) * mm, "end": v(3.39, 16.66) * mm});
            skLineSegment(sketch, "E6.87.2", {"start": v(3.99, 19.6) * mm, "end": v(3.39, 16.66) * mm});
            skLineSegment(sketch, "E6.87.3", {"start": v(4.33, 19.53) * mm, "end": v(3.99, 19.6) * mm});
            skLineSegment(sketch, "E6.88.0", {"start": v(2.51, 16.81) * mm, "end": v(2.96, 19.78) * mm});
            skLineSegment(sketch, "E6.88.1", {"start": v(2.51, 16.81) * mm, "end": v(2.22, 16.86) * mm});
            skLineSegment(sketch, "E6.88.2", {"start": v(2.61, 19.83) * mm, "end": v(2.22, 16.86) * mm});
            skLineSegment(sketch, "E6.88.3", {"start": v(2.96, 19.78) * mm, "end": v(2.61, 19.83) * mm});
            skLineSegment(sketch, "E6.89.0", {"start": v(1.33, 16.95) * mm, "end": v(1.57, 19.94) * mm});
            skLineSegment(sketch, "E6.89.1", {"start": v(1.33, 16.95) * mm, "end": v(1.04, 16.97) * mm});
            skLineSegment(sketch, "E6.89.2", {"start": v(1.22, 19.96) * mm, "end": v(1.04, 16.97) * mm});
            skLineSegment(sketch, "E6.89.3", {"start": v(1.57, 19.94) * mm, "end": v(1.22, 19.96) * mm});
            skSolve(sketch);
        }
        {
            var Q0;
            Q0 = qSketchRegion(id + "F3", true);
            extrude(context, id + "F4", {"entities" : qUnion([Q0]), "operationType" : NewBodyOperationType.REMOVE, "oppositeDirection" : true, "depth" : 25 * mm, "offsetDistance" : 25 * mm});
        }
        {
            var Q0;
            Q0=makeQuery(id+"F1.opExtrude","CAP_FACE",FACE,{"disambiguationData":[OSD([sQuery(id+"F0.wireOp",EDGE,"E0")])],"isStart":true});
            var sketch = newSketch(context, id + "F5", { "sketchPlane" : qUnion([Q0])});
            skArc(sketch, "E7", {"start": v(-2.6, 1.5) * mm, "mid": v(0, -3) * mm, "end": v(2.6, 1.5) * mm});
            skLineSegment(sketch, "E8", {"start": v(2.6, 1.5) * mm, "end": v(-2.6, 1.5) * mm});
            skSolve(sketch);
        }
        {
            var Q0;
            Q0 = qSketchRegion(id + "F5", true);
            extrude(context, id + "F6", {"entities" : qUnion([Q0]), "operationType" : NewBodyOperationType.REMOVE, "oppositeDirection" : true, "depth" : 9 * mm, "offsetDistance" : 25 * mm});
        }
    });
